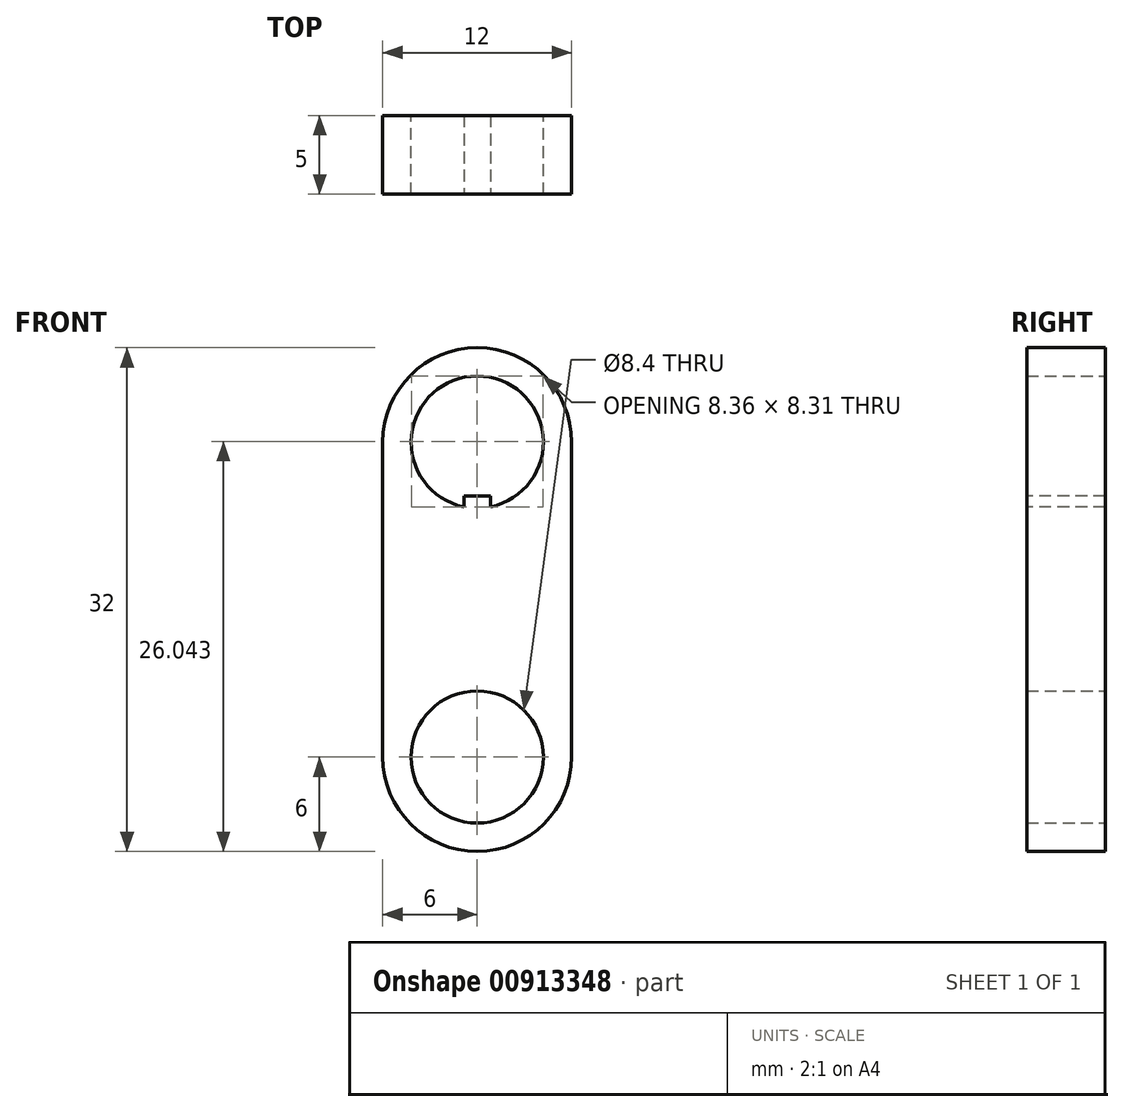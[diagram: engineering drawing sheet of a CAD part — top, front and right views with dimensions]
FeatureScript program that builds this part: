
annotation { "Feature Type Name" : "Feature", "Feature Type Description" : "" }
export const myFeature = defineFeature(function(context is Context, id is Id, definition is map)
    precondition{}
    {
        {
            var Q0;
            Q0=qCreatedBy(makeId("Front.planeOp"),FACE);
            var sketch = newSketch(context, id + "F0", { "sketchPlane" : qUnion([Q0])});
            skArc(sketch, "E0", {"start": v(-6, 0) * mm, "mid": v(0, -6) * mm, "end": v(6, 0) * mm});
            skArc(sketch, "E1", {"start": v(6, 20) * mm, "mid": v(0, 26) * mm, "end": v(-6, 20) * mm});
            skCircle(sketch, "E2", {"center": v(0, 20) * mm, "radius": 4.2 * mm});
            skCircle(sketch, "E3", {"center": v(0, 0) * mm, "radius": 4.2 * mm});
            skLineSegment(sketch, "E4", {"start": v(-6, 0) * mm, "end": v(-6, 20) * mm});
            skLineSegment(sketch, "E5.MirrorCS", {"start": v(6, 0) * mm, "end": v(6, 20) * mm});
            skSolve(sketch);
        }
        {
            var Q0;
            Q0 = qSketchRegion(id + "F0", true);
            extrude(context, id + "F1", {"entities" : qUnion([Q0]), "depth" : 5 * mm, "offsetDistance" : 25 * mm});
        }
        {
            var Q0;
            Q0=makeQuery(id+"F1.opExtrude","CAP_FACE",FACE,{"disambiguationData":[OSD([sQuery(id+"F0.wireOp",EDGE,"E0"),sQuery(id+"F0.wireOp",EDGE,"E1"),sQuery(id+"F0.wireOp",EDGE,"E2"),sQuery(id+"F0.wireOp",EDGE,"E3"),sQuery(id+"F0.wireOp",EDGE,"E4"),sQuery(id+"F0.wireOp",EDGE,"E5.MirrorCS")])],"isStart":false});
            var sketch = newSketch(context, id + "F2", { "sketchPlane" : qUnion([Q0])});
            skLineSegment(sketch, "E6", {"start": v(-0.85, 15.89) * mm, "end": v(-0.85, 16.59) * mm});
            skLineSegment(sketch, "E7", {"start": v(-0.85, 16.59) * mm, "end": v(0.85, 16.59) * mm});
            skLineSegment(sketch, "E8", {"start": v(0.85, 16.59) * mm, "end": v(0.85, 15.89) * mm});
            skLineSegment(sketch, "E9", {"start": v(0.85, 15.89) * mm, "end": v(0, 14.84) * mm});
            skLineSegment(sketch, "E10", {"start": v(0, 14.84) * mm, "end": v(-0.85, 15.89) * mm});
            skSolve(sketch);
        }
        {
            var Q0;
            Q0 = qSketchRegion(id + "F2", true);
            var Q1;
            Q1=makeQuery(id+"F1.opExtrude","CAP_FACE",FACE,{"disambiguationData":[OSD([sQuery(id+"F0.wireOp",EDGE,"E0"),sQuery(id+"F0.wireOp",EDGE,"E1"),sQuery(id+"F0.wireOp",EDGE,"E2"),sQuery(id+"F0.wireOp",EDGE,"E3"),sQuery(id+"F0.wireOp",EDGE,"E4"),sQuery(id+"F0.wireOp",EDGE,"E5.MirrorCS")])],"isStart":true});
            extrude(context, id + "F3", {"entities" : qUnion([Q0]), "operationType" : NewBodyOperationType.ADD, "endBound" : BoundingType.UP_TO_SURFACE, "oppositeDirection" : true, "depth" : 25 * mm, "endBoundEntityFace" : qUnion([Q1]), "offsetDistance" : 25 * mm});
        }
        {
            var Q0;
            Q0=qCreatedBy(makeId("Top.planeOp"),FACE);
            cPlane(context, id + "F4", {"entities" : qUnion([Q0]), "cplaneType" : CPlaneType.OFFSET, "offset" : 10 * mm, "width" : 150 * mm, "height" : 150 * mm});
        }
    });
